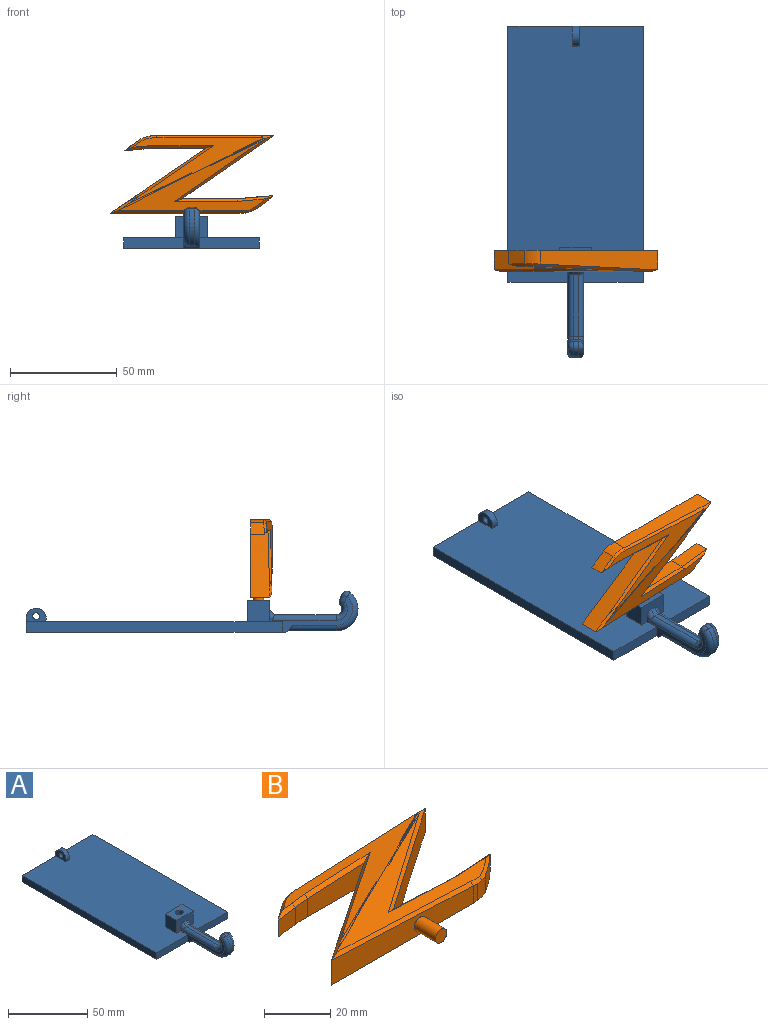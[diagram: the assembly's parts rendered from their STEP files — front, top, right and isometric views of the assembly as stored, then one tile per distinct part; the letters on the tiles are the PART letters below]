
ASSEMBLY  parts=2 mates=1
PART A: 45 faces, bbox 63.5x156.6x19.5 mm
  f0: plane 28x5mm, normal (0,-1,0), area 140mm2, adj f2,f3,f7,f14
  f1: plane 15x10mm, normal (0,-1,0), area 110.6mm2, adj f2,f8,f10,f12,f14,f16,f21,f24
  f2: plane 120x63.5mm, normal (0,0,1), area 7395.8mm2, adj f0,f1,f3,f4,f5,f6,f8,f9
  f3: plane 120x5mm, normal (1,0,0), area 600mm2, adj f0,f2,f4,f7
  f4: plane 63.5x5mm, normal (0,1,0), area 317.5mm2, adj f2,f3,f5,f7
  f5: plane 120x5mm, normal (-1,0,0), area 600mm2, adj f2,f4,f6,f7
  f6: plane 28x5mm, normal (0,-1,0), area 140mm2, adj f2,f5,f7,f16
  f7: plane 121.8x63.5mm, normal (0,0,-1), area 7633.5mm2, adj f0,f3,f4,f5,f6,f14,f16,f22
  f8: plane 10x10mm, normal (1,0,0), area 100mm2, adj f1,f2,f9,f12
  f9: plane 15x10mm, normal (0,1,0), area 150mm2, adj f2,f8,f10,f12
  f10: plane 10x10mm, normal (-1,0,0), area 100mm2, adj f1,f2,f9,f12
  f11: cylinder r=2.5mm len=10mm, axis (0,0,-1), area 157.1mm2, adj f12,f13
  f12: plane 15x10mm, normal (0,0,1), area 130.4mm2, adj f1,f8,f9,f10,f11
  f13: plane 5x5mm, normal (0,0,1), area 19.6mm2, adj f11
  f14: plane 39.18x16.8mm, normal (1,0,0), area 115.2mm2, adj f0,f1,f2,f7,f22,f23,f24,f25
  f15: plane 28.98x2.42mm, normal (0,0,1), area 70.1mm2, adj f19,f21,f26,f38
  f16: plane 39.18x16.8mm, normal (-1,0,0), area 115.2mm2, adj f1,f2,f6,f7,f22,f28,f32,f35
  f17: plane 2.47x2.42mm, normal (0,0.94,0.35), area 6.4mm2, adj f30,f31,f36,f37
  f18: plane 22.86x2.42mm, normal (0,0,-1), area 55.3mm2, adj f20,f22,f23,f28
  f19: cylinder r=2.7mm len=4.45mm, axis (-1,0,0), area 14.9mm2, adj f15,f29,f36,f40
  f20: cylinder r=10.2mm len=18.01mm, axis (-1,0,0), area 60.3mm2, adj f18,f25,f31,f32
  f21: plane 2.54x2.54mm, normal (0,-0.71,0.71), area 8.7mm2, adj f1,f15,f24,f35
  f22: plane 7.5x3.28mm, normal (0,-0.71,-0.71), area 11.7mm2, adj f7,f14,f16,f18,f23,f28
  f23: cylinder r=2.54mm len=22.86mm, axis (0,1,0), area 87.5mm2, adj f14,f18,f22,f25
  f24: cylinder r=2.54mm len=5.08mm, axis (0,0.71,0.71), area 12.2mm2, adj f1,f14,f21,f26
  f25: torus R=7.66mm, axis (-1,0,0), area 90.4mm2, adj f14,f20,f23,f27
  f26: cylinder r=2.54mm len=30.03mm, axis (0,1,0), area 117.1mm2, adj f14,f15,f24,f29
  f27: sphere r=2.54mm, area 12.3mm2, adj f25,f30,f31
  f28: cylinder r=2.54mm len=22.86mm, axis (0,-1,0), area 87.5mm2, adj f16,f18,f22,f32
  f29: torus R=5.24mm, axis (-1,0,0), area 32.9mm2, adj f14,f19,f26,f33
  f30: cylinder r=2.54mm len=3.37mm, axis (0,-0.35,0.94), area 10.5mm2, adj f14,f17,f27,f33
  f31: cylinder r=2.54mm len=4.01mm, axis (-1,0,0), area 11.7mm2, adj f17,f20,f27,f34
  f32: torus R=7.66mm, axis (-1,0,0), area 90.4mm2, adj f16,f20,f28,f34
  f33: sphere r=2.54mm, area 6.9mm2, adj f29,f30,f36
  f34: sphere r=2.54mm, area 12.3mm2, adj f31,f32,f37
  f35: cylinder r=2.54mm len=5.08mm, axis (0,0.71,0.71), area 12.2mm2, adj f1,f16,f21,f38
  f36: cylinder r=2.54mm len=2.54mm, axis (-1,0,0), area 6.5mm2, adj f17,f19,f33,f39
  f37: cylinder r=2.54mm len=3.37mm, axis (0,-0.35,0.94), area 10.5mm2, adj f16,f17,f34,f39
  f38: cylinder r=2.54mm len=30.03mm, axis (0,-1,0), area 117.1mm2, adj f15,f16,f35,f40
  f39: sphere r=2.54mm, area 6.9mm2, adj f36,f37,f40
  f40: torus R=5.24mm, axis (-1,0,0), area 32.9mm2, adj f16,f19,f38,f39
  f41: cylinder r=1.63mm len=3.26mm, axis (-1,0,0), area 32.5mm2, adj f43,f44
  f42: cylinder r=4.75mm len=9.5mm, axis (-1,0,0), area 58.1mm2, adj f2,f43,f44
  f43: plane 9.5x6.4mm, normal (1,0,0), area 42.5mm2, adj f2,f41,f42
  f44: plane 9.5x6.4mm, normal (-1,0,0), area 42.5mm2, adj f2,f41,f42
PART B: 39 faces, bbox 77.2x46.1x10.2 mm
  f0: cylinder r=4092.33mm len=45.09mm, axis (0,0,-1), area 464mm2, adj f6,f12,f19,f33,f35,f36
  f1: cylinder r=5687.07mm len=55.13mm, axis (0,0,-1), area 426.6mm2, adj f2,f18,f19,f22,f23
  f2: cylinder r=14.7mm len=7.17mm, axis (0,0,-1), area 46.5mm2, adj f1,f3,f19,f23,f25
  f3: cylinder r=98.78mm len=7.79mm, axis (0,0,-1), area 60.5mm2, adj f2,f4,f19,f27,f29
  f4: cylinder r=159.54mm len=8.25mm, axis (0,0,-1), area 52.3mm2, adj f3,f5,f19,f29,f31
  f5: cylinder r=42.85mm len=6.72mm, axis (0,0,-1), area 36.7mm2, adj f4,f6,f19,f31
  f6: cylinder r=655.68mm len=24.42mm, axis (0,0,-1), area 178.7mm2, adj f0,f5,f19,f33
  f7: plane 26.36x13.06mm, normal (0,0,1), area 9mm2, adj f9,f10,f20,f21,f22,f24
  f8: plane 33.85x17.31mm, normal (0,0,1), area 14.7mm2, adj f11,f20,f21,f36
  f9: cylinder r=5458.02mm len=24.74mm, axis (0,0,-1), area 0.6mm2, adj f7,f10,f20,f21
  f10: cylinder r=873.12mm len=13.82mm, axis (0,0,-1), area 0.3mm2, adj f7,f9,f20
  f11: cylinder r=873.12mm len=24.6mm, axis (0,0,-1), area 0.6mm2, adj f8,f20,f21
  f12: plane 60.8x9.01mm, normal (0,-1,0), area 450.1mm2, adj f0,f13,f19,f34,f36,f37
  f13: cylinder r=189.41mm len=6.42mm, axis (0,0,-1), area 12mm2, adj f12,f14,f19,f32
  f14: cylinder r=9.87mm len=6.58mm, axis (0,0,-1), area 30.7mm2, adj f13,f15,f19,f30,f32
  f15: cylinder r=45.28mm len=9.03mm, axis (0,0,-1), area 72.7mm2, adj f14,f16,f19,f28,f30
  f16: cylinder r=469.42mm len=16.76mm, axis (0,0,-1), area 110.6mm2, adj f15,f17,f19,f26,f28
  f17: cylinder r=891.99mm len=25.93mm, axis (0,0,-1), area 192.6mm2, adj f16,f18,f19,f26
  f18: cylinder r=2392.17mm len=43.33mm, axis (0,0,-1), area 447.8mm2, adj f1,f17,f19,f22,f24,f26
  f19: plane 76.6x36.43mm, normal (0,0,-1), area 1366mm2, adj f0,f1,f2,f3,f4,f5,f6,f12
  f20: plane 62.84x30.7mm, normal (-0.05,0.1,0.99), area 442.1mm2, adj f7,f8,f9,f10,f11,f21,f22,f23
  f21: plane 69.65x33.26mm, normal (0.04,-0.09,1), area 551.4mm2, adj f7,f8,f9,f11,f20,f24,f26,f28
  f22: cone r=5685.95mm half-angle=45deg, axis (0,0,-1), area 6.3mm2, adj f1,f7,f18,f20,f23,f24
  f23: bspline ~58.15x3.98mm, area 74.8mm2, adj f1,f2,f20,f22,f25
  f24: bspline ~46.5x32.47mm, area 79.2mm2, adj f7,f18,f21,f22,f26
  f25: bspline ~7.94x2.74mm, area 10.6mm2, adj f2,f20,f23,f27
  f26: bspline ~32.63x2.51mm, area 45.8mm2, adj f16,f17,f18,f21,f24,f28
  f27: bspline ~9.14x6.96mm, area 10.9mm2, adj f3,f20,f25,f29
  f28: bspline ~18.63x2.82mm, area 25.5mm2, adj f15,f16,f21,f26,f30
  f29: bspline ~8.42x2.06mm, area 10.8mm2, adj f3,f4,f20,f27,f31
  f30: bspline ~15.15x10.75mm, area 17.5mm2, adj f14,f15,f21,f28,f32
  f31: bspline ~5.8x1.57mm, area 9.4mm2, adj f4,f5,f20,f29,f33
  f32: bspline ~6.67x1.39mm, area 5.5mm2, adj f13,f14,f21,f30,f34
  f33: bspline ~31.03x2.64mm, area 43.6mm2, adj f0,f6,f20,f31,f35
  f34: plane 60.61x3.56mm, normal (0.03,-0.74,0.67), area 89.5mm2, adj f12,f21,f32,f36
  f35: bspline ~40.31x27.9mm, area 64mm2, adj f0,f20,f33,f36
  f36: cone r=4092.33mm half-angle=45deg, axis (0,0,1), area 18.8mm2, adj f0,f8,f12,f20,f21,f34,f35
  f37: cylinder r=2.48mm len=9mm, axis (0,1,0), area 140mm2, adj f12,f38
  f38: plane 4.95x4.95mm, normal (0,-1,0), area 19.2mm2, adj f37
PLACE A at identity
PLACE B rot(axis=(1,0,0),90deg) t=(4.03,-45.21,22.07)mm
MATE fastened B.f37 <-> A.f11  axis (0,0,-1) through (0,-48.88,7.54)mm
